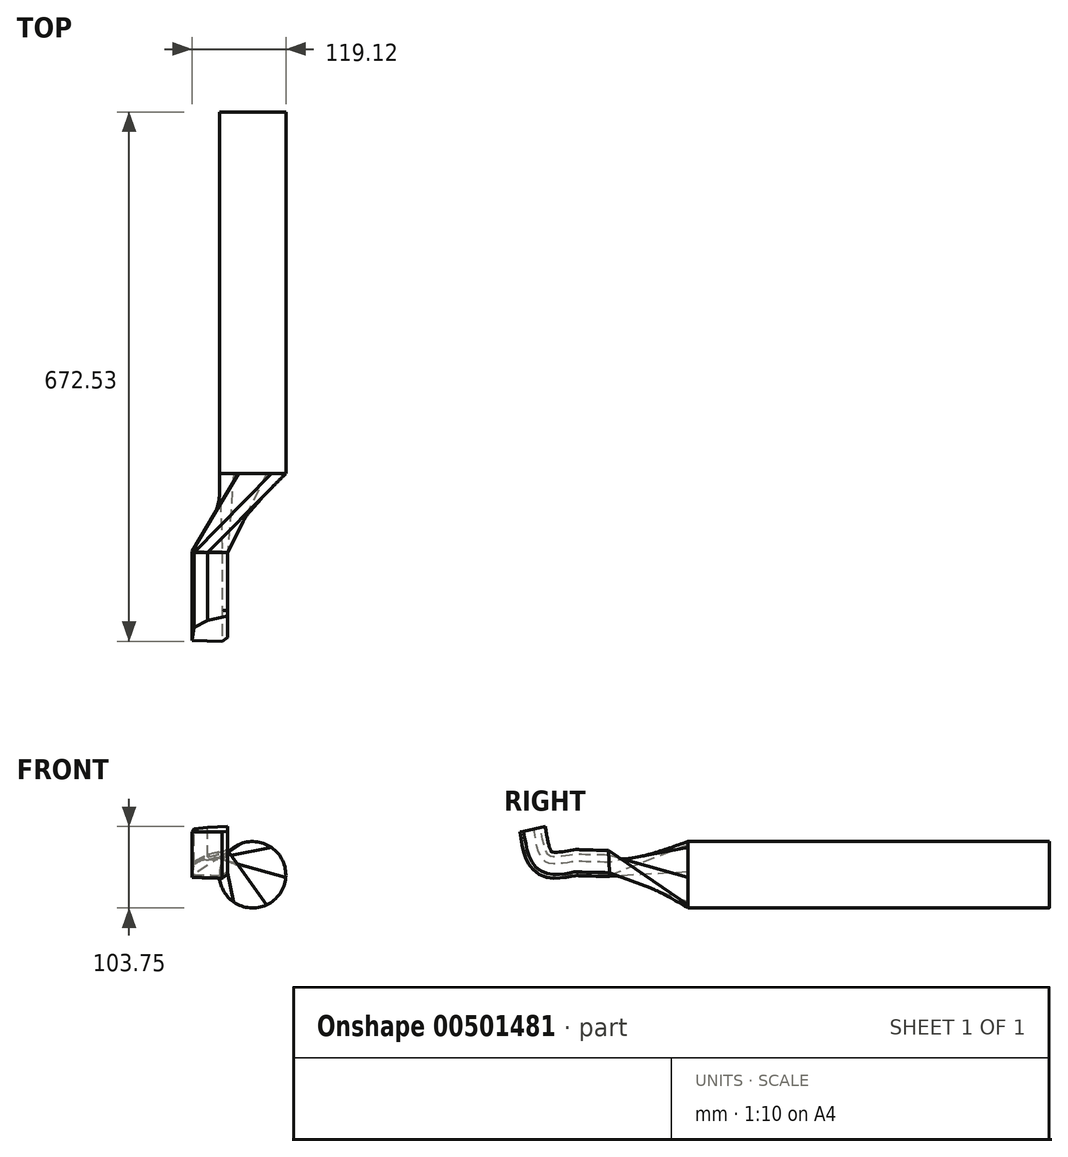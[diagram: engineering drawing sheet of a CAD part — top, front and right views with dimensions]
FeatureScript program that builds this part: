
annotation { "Feature Type Name" : "Feature", "Feature Type Description" : "" }
export const myFeature = defineFeature(function(context is Context, id is Id, definition is map)
    precondition{}
    {
        {
            var Q0;
            Q0=qCreatedBy(makeId("Front.planeOp"),FACE);
            var sketch = newSketch(context, id + "F0", { "sketchPlane" : qUnion([Q0])});
            skLineSegment(sketch, "E0", {"start": v(0, -29.11) * mm, "end": v(0, 0) * mm});
            skLineSegment(sketch, "E1", {"start": v(0, 0) * mm, "end": v(29.2, 0) * mm});
            skLineSegment(sketch, "E2", {"start": v(29.2, 0) * mm, "end": v(15.44, -10.56) * mm});
            skLineSegment(sketch, "E3", {"start": v(15.44, -10.56) * mm, "end": v(15.45, -31.8) * mm});
            skLineSegment(sketch, "E4", {"start": v(15.45, -31.8) * mm, "end": v(0.67, -27.76) * mm});
            skLineSegment(sketch, "E5", {"start": v(0.67, -27.76) * mm, "end": v(-7.07, -33.06) * mm});
            skLineSegment(sketch, "E6", {"start": v(-7.07, -33.06) * mm, "end": v(-45.28, -31.82) * mm});
            skLineSegment(sketch, "E7", {"start": v(-45.28, -31.82) * mm, "end": v(-42.47, -14.97) * mm});
            skLineSegment(sketch, "E8", {"start": v(-42.47, -14.97) * mm, "end": v(-25.57, -6.02) * mm});
            skLineSegment(sketch, "E9", {"start": v(0, 0) * mm, "end": v(-25.57, -6.02) * mm});
            skSolve(sketch);
        }
        {
            var Q0;
            Q0=qCreatedBy(makeId("Right.planeOp"),FACE);
            var sketch = newSketch(context, id + "F1", { "sketchPlane" : qUnion([Q0])});
            skFitSpline(sketch, "E10", {"points": [v(-62.54, 25.8) * mm, v(-44.35, -19.03) * mm, v(-8.13, -18.2) * mm, v(0, -18.18) * mm, v(17.84, -18.65) * mm, v(36.27, -19.13) * mm], "startDerivative": vector(30.84, -203.9) * mm, "endDerivative": vector(100.7, -3.09) * mm});
            skSolve(sketch);
        }
        {
            var Q0;
            {var subQ0=sQuery(id+"F0.wireOp",EDGE,"E6");Q0=makeQuery(id+"F0.imprint","IMPRINT",FACE,{"disambiguationData":[TD([[makeQuery(id+"F0.imprint","IMPRINT",EDGE,{"derivedFrom":subQ0}),-1.0]])]});}
            var Q1;
            Q1=sQuery(id+"F1.wireOp",EDGE,"E10");
            sweep(context, id + "F2", {"profiles" : qUnion([Q0]), "path" : qUnion([Q1])});
        }
        {
            var Q0;
            Q0=qCreatedBy(makeId("Front.planeOp"),FACE);
            cPlane(context, id + "F3", {"entities" : qUnion([Q0]), "cplaneType" : CPlaneType.OFFSET, "offset" : 136.07 * mm, "oppositeDirection" : true, "width" : 152.4 * mm, "height" : 152.4 * mm});
        }
        {
            var Q0;
            Q0=qCreatedBy(id+"F3.planeOp",FACE);
            var sketch = newSketch(context, id + "F4", { "sketchPlane" : qUnion([Q0])});
            skCircle(sketch, "E11", {"center": v(31.65, -31.8) * mm, "radius": 42.2 * mm});
            skSolve(sketch);
        }
        {
            var Q1;
            Q1=makeQuery(id+"F4.imprint","IMPRINT",FACE,{"disambiguationData":[TD([[makeQuery(id+"F4.imprint","IMPRINT",EDGE,{"derivedFrom":sQuery(id+"F4.wireOp",EDGE,"E11")}),1.0]])]});
            var Q2;
            Q2=makeQuery(id+"F2.opSweep","CAP_FACE",FACE,{"disambiguationData":[OSD([sQuery(id+"F0.wireOp",EDGE,"E0"),sQuery(id+"F0.wireOp",EDGE,"E5"),sQuery(id+"F0.wireOp",EDGE,"E6"),sQuery(id+"F0.wireOp",EDGE,"E7"),sQuery(id+"F0.wireOp",EDGE,"E8"),sQuery(id+"F0.wireOp",EDGE,"E9"),sQuery(id+"F1.wireOp",VERTEX,"E10.end")])],"isStart":true});
            loft(context, id + "F5", {"operationType" : NewBodyOperationType.ADD, "sheetProfilesArray" : [{ "sheetProfileEntities" : qUnion([Q1]) }, { "sheetProfileEntities" : qUnion([Q2]) }]});
        }
        {
            var Q0;
            Q0=makeQuery(id+"F5.opLoft","CAP_FACE",FACE,{"disambiguationData":[OSD([makeQuery(id+"F4.imprint","IMPRINT",FACE,{"disambiguationData":[TD([[makeQuery(id+"F4.imprint","IMPRINT",EDGE,{"derivedFrom":sQuery(id+"F4.wireOp",EDGE,"E11")}),1.0]])]})])],"isStart":true});
            extrude(context, id + "F6", {"entities" : qUnion([Q0]), "operationType" : NewBodyOperationType.ADD, "depth" : 459.4 * mm});
        }
    });
